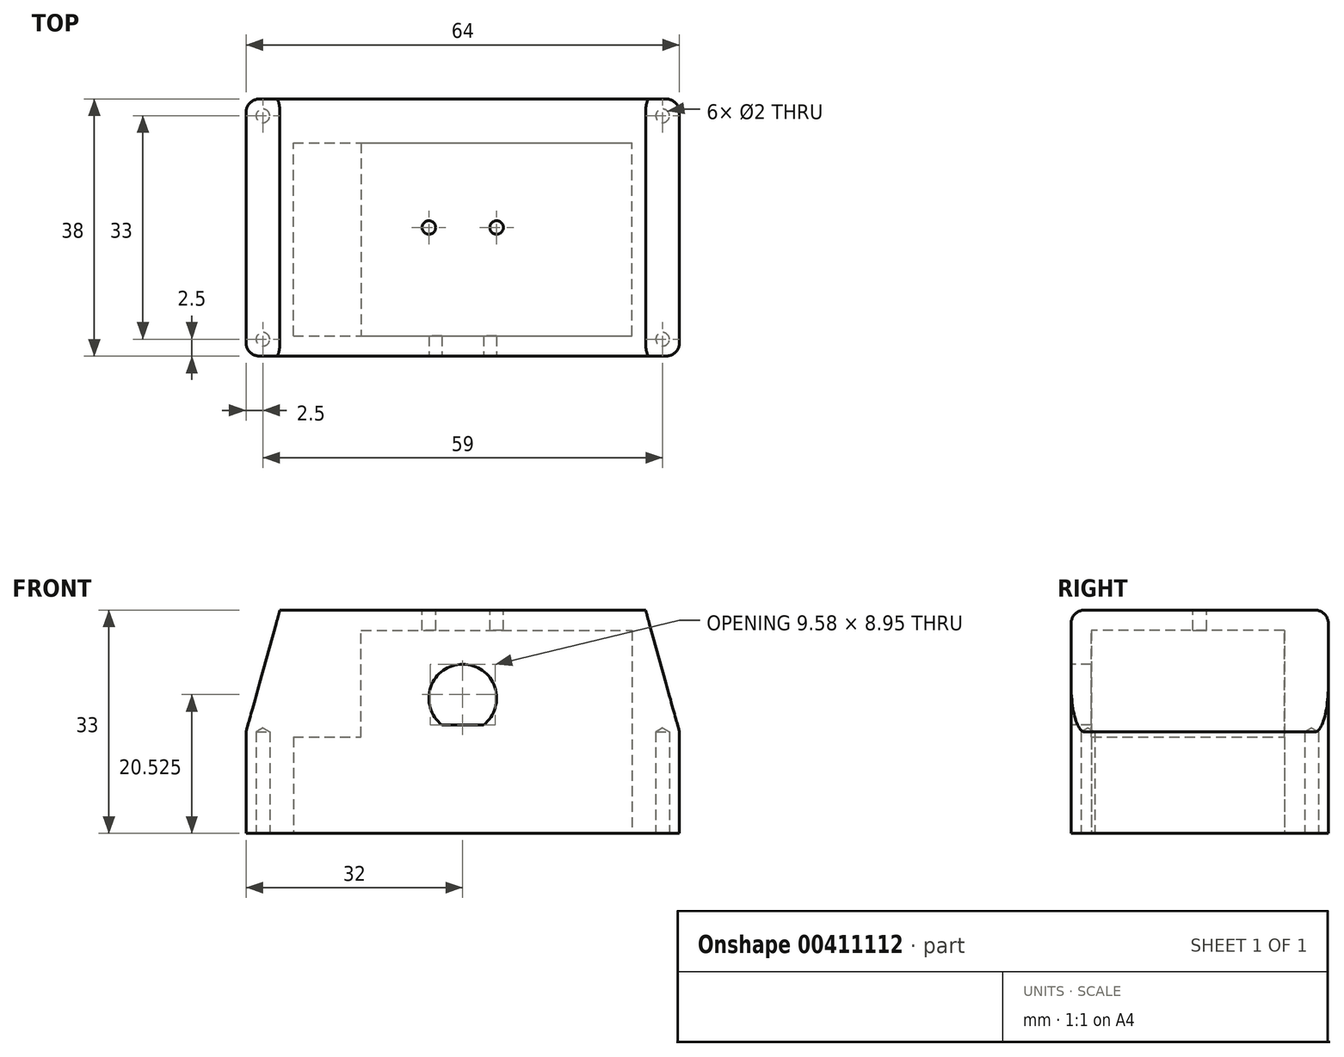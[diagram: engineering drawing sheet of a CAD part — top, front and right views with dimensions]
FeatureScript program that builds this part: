
annotation { "Feature Type Name" : "Feature", "Feature Type Description" : "" }
export const myFeature = defineFeature(function(context is Context, id is Id, definition is map)
    precondition{}
    {
        {
            var Q0;
            Q0=qCreatedBy(makeId("Top.planeOp"),FACE);
            var sketch = newSketch(context, id + "F0", { "sketchPlane" : qUnion([Q0])});
            skLineSegment(sketch, "E0.bottom", {"start": v(0, 0) * mm, "end": v(64, 0) * mm});
            skLineSegment(sketch, "E0.top", {"start": v(0, 38) * mm, "end": v(64, 38) * mm});
            skLineSegment(sketch, "E0.left", {"start": v(0, 0) * mm, "end": v(0, 38) * mm});
            skLineSegment(sketch, "E0.right", {"start": v(64, 0) * mm, "end": v(64, 38) * mm});
            skLineSegment(sketch, "E1.bottom", {"start": v(7, 3) * mm, "end": v(57, 3) * mm});
            skLineSegment(sketch, "E1.top", {"start": v(7, 31.5) * mm, "end": v(57, 31.5) * mm});
            skLineSegment(sketch, "E1.left", {"start": v(7, 3) * mm, "end": v(7, 31.5) * mm});
            skLineSegment(sketch, "E1.right", {"start": v(57, 3) * mm, "end": v(57, 31.5) * mm});
            skPoint(sketch, "E2", {"position": v(32, 38) * mm});
            skPoint(sketch, "E3", {"position": v(32, 31.5) * mm});
            skSolve(sketch);
        }
        {
            var Q0;
            Q0=makeQuery(id+"F0.imprint","IMPRINT",FACE,{"disambiguationData":[TD([[makeQuery(id+"F0.imprint","IMPRINT",EDGE,{"derivedFrom":sQuery(id+"F0.wireOp",EDGE,"E0.bottom")}),1.0]])]});
            extrude(context, id + "F1", {"entities" : qUnion([Q0]), "depth" : 30 * mm});
        }
        {
            var Q0;
            Q0=makeQuery(id+"F1.opExtrude","CAP_FACE",FACE,{"disambiguationData":[OSD([sQuery(id+"F0.wireOp",EDGE,"E0.bottom"),sQuery(id+"F0.wireOp",EDGE,"E0.top"),sQuery(id+"F0.wireOp",EDGE,"E0.left"),sQuery(id+"F0.wireOp",EDGE,"E0.right"),sQuery(id+"F0.wireOp",EDGE,"E1.bottom"),sQuery(id+"F0.wireOp",EDGE,"E1.top"),sQuery(id+"F0.wireOp",EDGE,"E1.left"),sQuery(id+"F0.wireOp",EDGE,"E1.right")])],"isStart":true});
            var sketch = newSketch(context, id + "F2", { "sketchPlane" : qUnion([Q0])});
            skLineSegment(sketch, "E4.bottom", {"start": v(2.5, -35.5) * mm, "end": v(61.5, -35.5) * mm, "construction": true});
            skLineSegment(sketch, "E4.top", {"start": v(2.5, -2.5) * mm, "end": v(61.5, -2.5) * mm, "construction": true});
            skLineSegment(sketch, "E4.left", {"start": v(2.5, -35.5) * mm, "end": v(2.5, -2.5) * mm, "construction": true});
            skLineSegment(sketch, "E4.right", {"start": v(61.5, -35.5) * mm, "end": v(61.5, -2.5) * mm, "construction": true});
            skSolve(sketch);
        }
        {
            var Q0;
            Q0=sQuery(id+"F2.wireOp",VERTEX,"E4.left.end");
            var Q1;
            Q1=sQuery(id+"F2.wireOp",VERTEX,"E4.top.end");
            var Q2;
            Q2=sQuery(id+"F2.wireOp",VERTEX,"E4.right.start");
            var Q3;
            Q3=sQuery(id+"F2.wireOp",VERTEX,"E4.left.start");
            var Q4;
            Q4=makeQuery(id+"F1.opExtrude","SWEPT_BODY",BODY,{"disambiguationData":[OSD([sQuery(id+"F0.wireOp",EDGE,"E0.bottom"),sQuery(id+"F0.wireOp",EDGE,"E0.top"),sQuery(id+"F0.wireOp",EDGE,"E0.left"),sQuery(id+"F0.wireOp",EDGE,"E0.right"),sQuery(id+"F0.wireOp",EDGE,"E1.bottom"),sQuery(id+"F0.wireOp",EDGE,"E1.top"),sQuery(id+"F0.wireOp",EDGE,"E1.left"),sQuery(id+"F0.wireOp",EDGE,"E1.right")])]});
            hole(context, id + "F3", {"style" : HoleStyle.SIMPLE, "endStyle" : HoleEndStyle.BLIND, "holeDiameter" : 2 * mm, "holeDepth" : 15 * mm, "isTappedThrough" : true, "tappedDepth" : 12 * mm, "tapClearance" : 3, "locations" : qUnion([Q0, Q1, Q2, Q3]), "scope" : qUnion([Q4])});
        }
        {
            var Q0;
            Q0=makeQuery(id+"F1.opExtrude","CAP_FACE",FACE,{"disambiguationData":[OSD([sQuery(id+"F0.wireOp",EDGE,"E0.bottom"),sQuery(id+"F0.wireOp",EDGE,"E0.top"),sQuery(id+"F0.wireOp",EDGE,"E0.left"),sQuery(id+"F0.wireOp",EDGE,"E0.right"),sQuery(id+"F0.wireOp",EDGE,"E1.bottom"),sQuery(id+"F0.wireOp",EDGE,"E1.top"),sQuery(id+"F0.wireOp",EDGE,"E1.left"),sQuery(id+"F0.wireOp",EDGE,"E1.right")])],"isStart":false});
            var sketch = newSketch(context, id + "F4", { "sketchPlane" : qUnion([Q0])});
            skLineSegment(sketch, "E5.bottom", {"start": v(0, 0) * mm, "end": v(64, 0) * mm});
            skLineSegment(sketch, "E5.top", {"start": v(0, 38) * mm, "end": v(64, 38) * mm});
            skLineSegment(sketch, "E5.left", {"start": v(0, 0) * mm, "end": v(0, 38) * mm});
            skLineSegment(sketch, "E5.right", {"start": v(64, 0) * mm, "end": v(64, 38) * mm});
            skSolve(sketch);
        }
        {
            var Q0;
            Q0 = qSketchRegion(id + "F4", true);
            extrude(context, id + "F5", {"entities" : qUnion([Q0]), "operationType" : NewBodyOperationType.ADD, "depth" : 3 * mm});
        }
        {
            var Q0;
            Q0=makeQuery(id+"F5.opExtrude","CAP_FACE",FACE,{"disambiguationData":[OSD([sQuery(id+"F4.wireOp",EDGE,"E5.bottom"),sQuery(id+"F4.wireOp",EDGE,"E5.top"),sQuery(id+"F4.wireOp",EDGE,"E5.left"),sQuery(id+"F4.wireOp",EDGE,"E5.right")])],"isStart":true});
            var sketch = newSketch(context, id + "F6", { "sketchPlane" : qUnion([Q0])});
            skLineSegment(sketch, "E6.bottom", {"start": v(7, -31.5) * mm, "end": v(17, -31.5) * mm});
            skLineSegment(sketch, "E6.top", {"start": v(7, -3) * mm, "end": v(17, -3) * mm});
            skLineSegment(sketch, "E6.left", {"start": v(7, -31.5) * mm, "end": v(7, -3) * mm});
            skLineSegment(sketch, "E6.right", {"start": v(17, -31.5) * mm, "end": v(17, -3) * mm});
            skSolve(sketch);
        }
        {
            var Q0;
            Q0=makeQuery(id+"F1.opExtrude","CAP_FACE",FACE,{"disambiguationData":[OSD([sQuery(id+"F0.wireOp",EDGE,"E0.bottom"),sQuery(id+"F0.wireOp",EDGE,"E0.top"),sQuery(id+"F0.wireOp",EDGE,"E0.left"),sQuery(id+"F0.wireOp",EDGE,"E0.right"),sQuery(id+"F0.wireOp",EDGE,"E1.bottom"),sQuery(id+"F0.wireOp",EDGE,"E1.top"),sQuery(id+"F0.wireOp",EDGE,"E1.left"),sQuery(id+"F0.wireOp",EDGE,"E1.right")])],"isStart":true});
            cPlane(context, id + "F7", {"entities" : qUnion([Q0]), "cplaneType" : CPlaneType.OFFSET, "offset" : 14.25 * mm, "oppositeDirection" : true, "width" : 150 * mm, "height" : 150 * mm});
        }
        {
            var Q0;
            Q0=makeQuery(id+"F6.imprint","IMPRINT",FACE,{"disambiguationData":[TD([[makeQuery(id+"F6.imprint","IMPRINT",EDGE,{"derivedFrom":sQuery(id+"F6.wireOp",EDGE,"E6.bottom")}),1.0]])]});
            var Q1;
            Q1=qCreatedBy(id+"F7.planeOp",FACE);
            extrude(context, id + "F8", {"entities" : qUnion([Q0]), "operationType" : NewBodyOperationType.ADD, "endBound" : BoundingType.UP_TO_SURFACE, "endBoundEntityFace" : qUnion([Q1]), "depth" : 25 * mm});
        }
        {
            var Q0;
            Q0=makeQuery(id+"F5.boolean.opBoolean","MERGE",FACE,{"derivedFrom":[makeQuery(id+"F1.opExtrude","SWEPT_FACE",FACE,{"disambiguationData":[OSD([sQuery(id+"F0.wireOp",EDGE,"E0.bottom")])]}),makeQuery(id+"F5.opExtrude","SWEPT_FACE",FACE,{"disambiguationData":[OSD([sQuery(id+"F4.wireOp",EDGE,"E5.bottom")])]})]});
            var sketch = newSketch(context, id + "F9", { "sketchPlane" : qUnion([Q0])});
            skLineSegment(sketch, "E7", {"start": v(0, 15) * mm, "end": v(0, 33) * mm});
            skLineSegment(sketch, "E8", {"start": v(0, 33) * mm, "end": v(5, 33) * mm});
            skLineSegment(sketch, "E9", {"start": v(5, 33) * mm, "end": v(0, 15) * mm});
            skLineSegment(sketch, "E10", {"start": v(64, 15) * mm, "end": v(64, 33) * mm});
            skLineSegment(sketch, "E11", {"start": v(64, 33) * mm, "end": v(59, 33) * mm});
            skLineSegment(sketch, "E12", {"start": v(59, 33) * mm, "end": v(64, 15) * mm});
            skSolve(sketch);
        }
        {
            var Q0;
            Q0=makeQuery(id+"F9.imprint","IMPRINT",FACE,{"disambiguationData":[TD([[makeQuery(id+"F9.imprint","IMPRINT",EDGE,{"derivedFrom":sQuery(id+"F9.wireOp",EDGE,"E7")}),1.0]])]});
            var Q1;
            Q1=makeQuery(id+"F9.imprint","IMPRINT",FACE,{"disambiguationData":[TD([[makeQuery(id+"F9.imprint","IMPRINT",EDGE,{"derivedFrom":sQuery(id+"F9.wireOp",EDGE,"E10")}),-1.0]])]});
            var Q2;
            Q2=makeQuery(id+"F5.boolean.opBoolean","MERGE",FACE,{"derivedFrom":[makeQuery(id+"F1.opExtrude","SWEPT_FACE",FACE,{"disambiguationData":[OSD([sQuery(id+"F0.wireOp",EDGE,"E0.top")])]}),makeQuery(id+"F5.opExtrude","SWEPT_FACE",FACE,{"disambiguationData":[OSD([sQuery(id+"F4.wireOp",EDGE,"E5.top")])]})]});
            extrude(context, id + "F10", {"entities" : qUnion([Q0, Q1]), "operationType" : NewBodyOperationType.REMOVE, "endBound" : BoundingType.UP_TO_SURFACE, "oppositeDirection" : true, "endBoundEntityFace" : qUnion([Q2]), "depth" : 25 * mm});
        }
        {
            var Q0;
            Q0=makeQuery(id+"F5.boolean.opBoolean","MERGE",EDGE,{"derivedFrom":[makeQuery(id+"F1.opExtrude","SWEPT_EDGE",EDGE,{"disambiguationData":[OSD([sQuery(id+"F0.wireOp",EDGE,"E0.bottom"),sQuery(id+"F0.wireOp",EDGE,"E0.left")])]}),makeQuery(id+"F5.opExtrude","SWEPT_EDGE",EDGE,{"disambiguationData":[OSD([sQuery(id+"F4.wireOp",EDGE,"E5.bottom"),sQuery(id+"F4.wireOp",EDGE,"E5.left")])]})]});
            var Q1;
            Q1=makeQuery(id+"F10.boolean.opBoolean","COPY",EDGE,{"derivedFrom":makeQuery(id+"F10.opExtrude","CAP_EDGE",EDGE,{"disambiguationData":[OSD([sQuery(id+"F9.wireOp",EDGE,"E9")])],"isStart":true})});
            var Q2;
            Q2=makeQuery(id+"F10.boolean.opBoolean","COPY",EDGE,{"derivedFrom":makeQuery(id+"F10.opExtrude","CAP_EDGE",EDGE,{"disambiguationData":[OSD([sQuery(id+"F9.wireOp",EDGE,"E12")])],"isStart":true})});
            var Q3;
            Q3=makeQuery(id+"F5.boolean.opBoolean","MERGE",EDGE,{"derivedFrom":[makeQuery(id+"F1.opExtrude","SWEPT_EDGE",EDGE,{"disambiguationData":[OSD([sQuery(id+"F0.wireOp",EDGE,"E0.bottom"),sQuery(id+"F0.wireOp",EDGE,"E0.right")])]}),makeQuery(id+"F5.opExtrude","SWEPT_EDGE",EDGE,{"disambiguationData":[OSD([sQuery(id+"F4.wireOp",EDGE,"E5.bottom"),sQuery(id+"F4.wireOp",EDGE,"E5.right")])]})]});
            var Q4;
            Q4=makeQuery(id+"F10.boolean.opBoolean","COPY",EDGE,{"derivedFrom":makeQuery(id+"F10.opExtrude","CAP_EDGE",EDGE,{"disambiguationData":[OSD([sQuery(id+"F9.wireOp",EDGE,"E9")])],"isStart":false})});
            var Q5;
            Q5=makeQuery(id+"F5.boolean.opBoolean","MERGE",EDGE,{"derivedFrom":[makeQuery(id+"F1.opExtrude","SWEPT_EDGE",EDGE,{"disambiguationData":[OSD([sQuery(id+"F0.wireOp",EDGE,"E0.top"),sQuery(id+"F0.wireOp",EDGE,"E0.left")])]}),makeQuery(id+"F5.opExtrude","SWEPT_EDGE",EDGE,{"disambiguationData":[OSD([sQuery(id+"F4.wireOp",EDGE,"E5.top"),sQuery(id+"F4.wireOp",EDGE,"E5.left")])]})]});
            var Q6;
            Q6=makeQuery(id+"F5.boolean.opBoolean","MERGE",EDGE,{"derivedFrom":[makeQuery(id+"F1.opExtrude","SWEPT_EDGE",EDGE,{"disambiguationData":[OSD([sQuery(id+"F0.wireOp",EDGE,"E0.top"),sQuery(id+"F0.wireOp",EDGE,"E0.right")])]}),makeQuery(id+"F5.opExtrude","SWEPT_EDGE",EDGE,{"disambiguationData":[OSD([sQuery(id+"F4.wireOp",EDGE,"E5.top"),sQuery(id+"F4.wireOp",EDGE,"E5.right")])]})]});
            var Q7;
            Q7=makeQuery(id+"F10.boolean.opBoolean","COPY",EDGE,{"derivedFrom":makeQuery(id+"F10.opExtrude","CAP_EDGE",EDGE,{"disambiguationData":[OSD([sQuery(id+"F9.wireOp",EDGE,"E12")])],"isStart":false})});
            var Q8;
            Q8=makeQuery(id+"F5.opExtrude","CAP_EDGE",EDGE,{"disambiguationData":[OSD([sQuery(id+"F4.wireOp",EDGE,"E5.bottom")])],"isStart":false});
            var Q9;
            Q9=makeQuery(id+"F10.boolean.opBoolean","COPY",EDGE,{"derivedFrom":makeQuery(id+"F10.opExtrude","SWEPT_EDGE",EDGE,{"disambiguationData":[OSD([sQuery(id+"F4.wireOp",EDGE,"E5.bottom"),sQuery(id+"F9.wireOp",EDGE,"E8"),sQuery(id+"F9.wireOp",EDGE,"E9")])]})});
            var Q10;
            Q10=makeQuery(id+"F5.opExtrude","CAP_EDGE",EDGE,{"disambiguationData":[OSD([sQuery(id+"F4.wireOp",EDGE,"E5.top")])],"isStart":false});
            var Q11;
            Q11=makeQuery(id+"F10.boolean.opBoolean","COPY",EDGE,{"derivedFrom":makeQuery(id+"F10.opExtrude","SWEPT_EDGE",EDGE,{"disambiguationData":[OSD([sQuery(id+"F4.wireOp",EDGE,"E5.bottom"),sQuery(id+"F9.wireOp",EDGE,"E11"),sQuery(id+"F9.wireOp",EDGE,"E12")])]})});
            fillet(context, id + "F11", {"entities" : qUnion([Q0, Q1, Q2, Q3, Q4, Q5, Q6, Q7, Q8, Q9, Q10, Q11]), "radius" : 2 * mm, "tangentPropagation" : true, "allowEdgeOverflow" : false});
        }
        {
            var Q0;
            Q0=makeQuery(id+"F5.boolean.opBoolean","MERGE",FACE,{"derivedFrom":[makeQuery(id+"F1.opExtrude","SWEPT_FACE",FACE,{"disambiguationData":[OSD([sQuery(id+"F0.wireOp",EDGE,"E0.bottom")])]}),makeQuery(id+"F5.opExtrude","SWEPT_FACE",FACE,{"disambiguationData":[OSD([sQuery(id+"F4.wireOp",EDGE,"E5.bottom")])]})]});
            var sketch = newSketch(context, id + "F12", { "sketchPlane" : qUnion([Q0])});
            skArc(sketch, "E13", {"start": v(35.07, 16.05) * mm, "mid": v(32, 25) * mm, "end": v(28.93, 16.05) * mm});
            skLineSegment(sketch, "E14", {"start": v(28.93, 16.05) * mm, "end": v(35.07, 16.05) * mm});
            skSolve(sketch);
        }
        {
            var Q0;
            Q0=makeQuery(id+"F12.imprint","IMPRINT",FACE,{"disambiguationData":[TD([[makeQuery(id+"F12.imprint","IMPRINT",EDGE,{"derivedFrom":sQuery(id+"F12.wireOp",EDGE,"E13")}),1.0]])]});
            var Q1;
            Q1=makeQuery(id+"F1.opExtrude","SWEPT_FACE",FACE,{"disambiguationData":[OSD([sQuery(id+"F0.wireOp",EDGE,"E1.bottom")])]});
            extrude(context, id + "F13", {"entities" : qUnion([Q0]), "operationType" : NewBodyOperationType.REMOVE, "endBound" : BoundingType.UP_TO_SURFACE, "oppositeDirection" : true, "endBoundEntityFace" : qUnion([Q1]), "depth" : 25 * mm});
        }
        {
            var Q0;
            Q0=makeQuery(id+"F5.opExtrude","CAP_FACE",FACE,{"disambiguationData":[OSD([sQuery(id+"F4.wireOp",EDGE,"E5.bottom"),sQuery(id+"F4.wireOp",EDGE,"E5.top"),sQuery(id+"F4.wireOp",EDGE,"E5.left"),sQuery(id+"F4.wireOp",EDGE,"E5.right")])],"isStart":false});
            var sketch = newSketch(context, id + "F14", { "sketchPlane" : qUnion([Q0])});
            skLineSegment(sketch, "E15", {"start": v(6.52, 19) * mm, "end": v(57.48, 19) * mm, "construction": true});
            skPoint(sketch, "E16", {"position": v(32, 19) * mm});
            skPoint(sketch, "E17", {"position": v(37, 19) * mm});
            skPoint(sketch, "E18", {"position": v(27, 19) * mm});
            skSolve(sketch);
        }
        {
            var Q0;
            Q0=sQuery(id+"F14.wireOp",VERTEX,"E18");
            var Q1;
            Q1=sQuery(id+"F14.wireOp",VERTEX,"E17");
            var Q2;
            Q2=makeQuery(id+"F1.opExtrude","SWEPT_BODY",BODY,{"disambiguationData":[OSD([sQuery(id+"F0.wireOp",EDGE,"E0.bottom"),sQuery(id+"F0.wireOp",EDGE,"E0.top"),sQuery(id+"F0.wireOp",EDGE,"E0.left"),sQuery(id+"F0.wireOp",EDGE,"E0.right"),sQuery(id+"F0.wireOp",EDGE,"E1.bottom"),sQuery(id+"F0.wireOp",EDGE,"E1.top"),sQuery(id+"F0.wireOp",EDGE,"E1.left"),sQuery(id+"F0.wireOp",EDGE,"E1.right")])]});
            hole(context, id + "F15", {"style" : HoleStyle.SIMPLE, "endStyle" : HoleEndStyle.THROUGH, "holeDiameter" : 2 * mm, "isTappedThrough" : true, "tappedDepth" : 12 * mm, "tapClearance" : 3, "locations" : qUnion([Q0, Q1]), "scope" : qUnion([Q2])});
        }
    });
